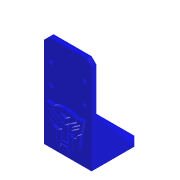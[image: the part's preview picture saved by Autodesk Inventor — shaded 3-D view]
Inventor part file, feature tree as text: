
AUTODESK INVENTOR PART (.ipt)
format: ipt  version: 2022 (Build 260153000, 153)  size: 575,488 bytes
history: native  units: mm
features: sketch x7, extrude x4, hole x2, other x2, rib x1, mirror x1, chamfer x1
ambient origin geometry x8: Origin, YZ Plane, XZ Plane, XY Plane, X Axis, Y Axis, Z Axis, Center Point
bodies: Solid1 (feature_tree)
feature tree (18):
  extrude  "Extrusion1"  Depth=30.0mm
  hole  "Camera Mounting Holes"  [1 undecoded]
  extrude  "Extrusion2"  Depth=4.0mm
  hole  "Mounting Holes"  [1 undecoded]
  rib  "Rib1"
  mirror  "Mirror1"
  chamfer  "Chamfer1"  Distance=3.0mm
  extrude  "Decepticon Logo"  Depth=2.0mm
  extrude  "Autobots Logo"  Depth=2.0mm
  sketch  "Sketch1"  dims[d0=30.0mm d1=30.0mm]
  sketch  "Sketch2"  dims[d2=3.0mm d3=0.0mm d4=21.0mm]
  sketch  "Sketch5"  dims[d5=13.0mm d6=4.0mm]
  sketch  "Sketch6"  dims[d7=2.4mm d8=6.0mm d9=4.0mm d10=2.0mm d11=90.0deg d12=6.0mm d13=0.0mm d15=30.0mm]
  sketch  "Sketch7"  dims[d16=30.0mm]
  sketch  "Sketch8"  dims[d17=3.0mm]
  other  "Image1"
  sketch  "Sketch10"  dims[d18=3.0mm d19=3.0mm d20=0.0mm d21=15.0mm d22=13.5mm d23=7.0mm d24=3.4mm d25=6.0mm d26=4.0mm d27=2.0mm d28=90.0deg d29=6.0mm d30=0.0mm d31=22.0mm d35=1.0mm d36=2.0mm d37=0.0mm d38=0.0mm d39=1.0mm d40=1.0mm d41=27.0mm d42=32.0mm d43=3.0mm d44=2.0mm d45=45.0deg d71=2.0mm d72=0.0mm d75=5.5mm d157=2.0mm d158=0.0mm d73=0.5mm d74=0.872665mm]
  other  "Image2"
note: 2 required parameter values undecoded (feature->parameter linkage not recoverable at this tier; creation-order binding heuristic only, values carry confidence <= 0.55)
